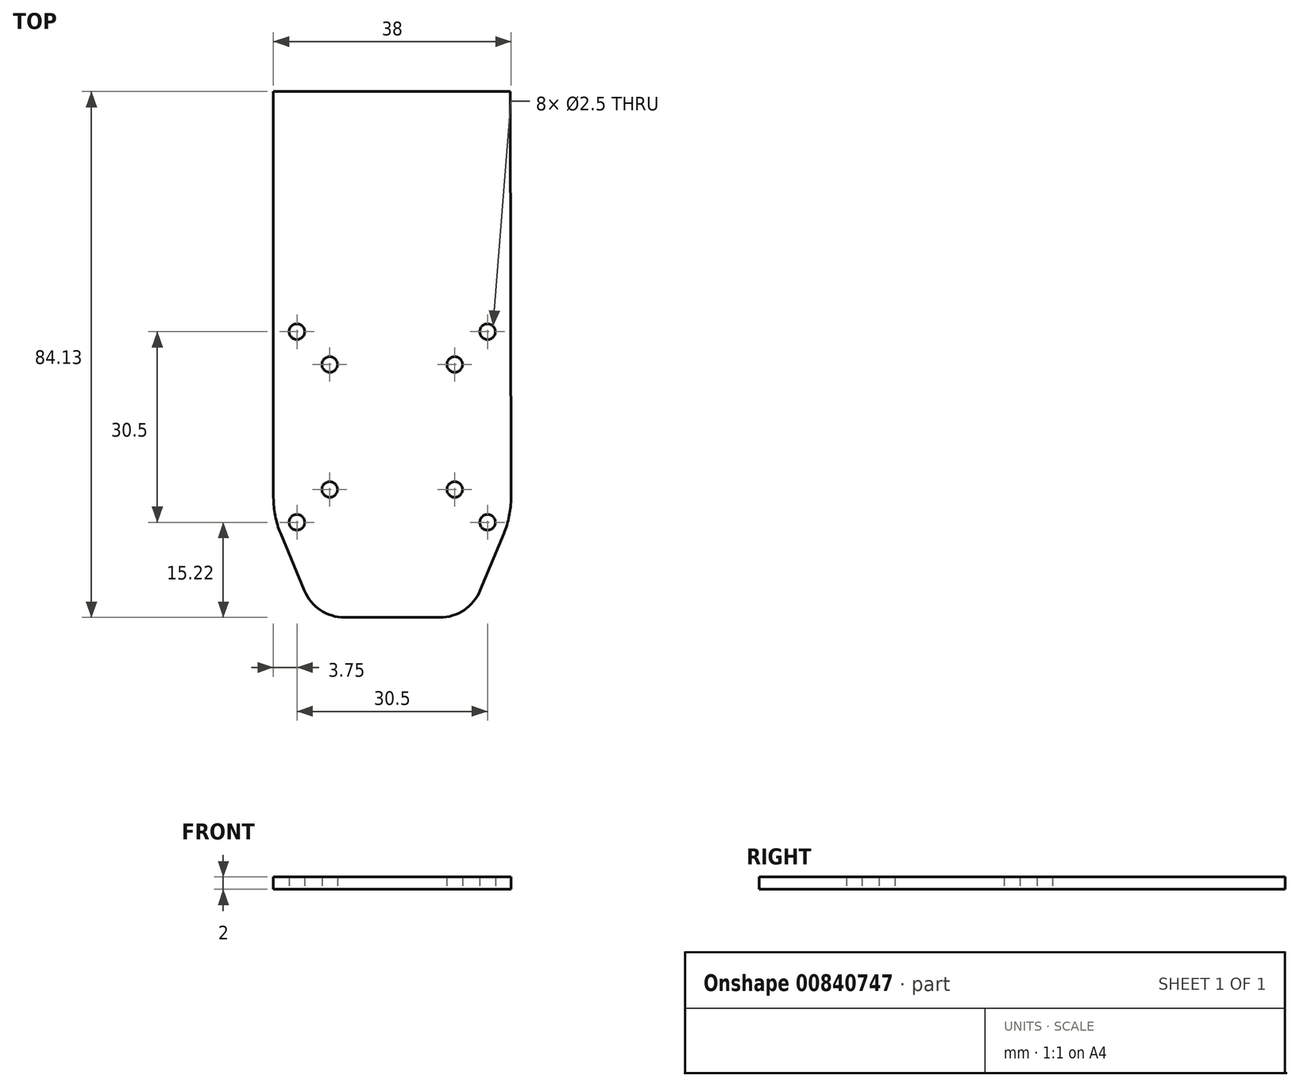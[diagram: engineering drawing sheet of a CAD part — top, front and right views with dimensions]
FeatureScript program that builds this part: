
annotation { "Feature Type Name" : "Feature", "Feature Type Description" : "" }
export const myFeature = defineFeature(function(context is Context, id is Id, definition is map)
    precondition{}
    {
        {
            var Q0;
            Q0=qCreatedBy(makeId("Top.planeOp"),FACE);
            var sketch = newSketch(context, id + "F0", { "sketchPlane" : qUnion([Q0])});
            skLineSegment(sketch, "E0.bottom", {"start": v(10, -10) * mm, "end": v(-10, -10) * mm, "construction": true});
            skLineSegment(sketch, "E0.top", {"start": v(10, 10) * mm, "end": v(-10, 10) * mm, "construction": true});
            skLineSegment(sketch, "E0.left", {"start": v(10, -10) * mm, "end": v(10, 10) * mm, "construction": true});
            skLineSegment(sketch, "E0.right", {"start": v(-10, -10) * mm, "end": v(-10, 10) * mm, "construction": true});
            skPoint(sketch, "E0.middle", {"position": v(0, 0) * mm});
            skCircle(sketch, "E1", {"center": v(-10, 10) * mm, "radius": 1.25 * mm});
            skCircle(sketch, "E2.MirrorC", {"center": v(10, 10) * mm, "radius": 1.25 * mm});
            skCircle(sketch, "E3.MirrorC", {"center": v(10, -10) * mm, "radius": 1.25 * mm});
            skCircle(sketch, "E4.MirrorC", {"center": v(-10, -10) * mm, "radius": 1.25 * mm});
            skPoint(sketch, "E5.right.end.orphan", {"position": v(-13.5, 13.5) * mm});
            skPoint(sketch, "E5.bottom.end.orphan", {"position": v(-13.5, -13.5) * mm});
            skPoint(sketch, "E5.left.end.orphan", {"position": v(13.5, 13.5) * mm});
            skPoint(sketch, "E5.left.start.orphan", {"position": v(13.5, -13.5) * mm});
            skLineSegment(sketch, "E6.bottom", {"start": v(15.25, -15.25) * mm, "end": v(-15.25, -15.25) * mm, "construction": true});
            skLineSegment(sketch, "E6.top", {"start": v(15.25, 15.25) * mm, "end": v(-15.25, 15.25) * mm, "construction": true});
            skLineSegment(sketch, "E6.left", {"start": v(15.25, -15.25) * mm, "end": v(15.25, 15.25) * mm, "construction": true});
            skLineSegment(sketch, "E6.right", {"start": v(-15.25, -15.25) * mm, "end": v(-15.25, 15.25) * mm, "construction": true});
            skCircle(sketch, "E7", {"center": v(-15.25, 15.25) * mm, "radius": 1.25 * mm});
            skCircle(sketch, "E8.MirrorC", {"center": v(15.25, 15.25) * mm, "radius": 1.25 * mm});
            skCircle(sketch, "E9.MirrorC", {"center": v(15.25, -15.25) * mm, "radius": 1.25 * mm});
            skCircle(sketch, "E10.MirrorC", {"center": v(-15.25, -15.25) * mm, "radius": 1.25 * mm});
            skLineSegment(sketch, "E11.top", {"start": v(-19, 53.66) * mm, "end": v(18.87, 53.66) * mm});
            skLineSegment(sketch, "E12", {"start": v(-17.85, -17.05) * mm, "end": v(-14.07, -26.15) * mm});
            skLineSegment(sketch, "E13.MirrorCS", {"start": v(17.85, -17.05) * mm, "end": v(14.07, -26.15) * mm});
            skPoint(sketch, "E14.visualSharp", {"position": v(-19, -14.28) * mm});
            skArc(sketch, "E14.filletArc", {"start": v(-19, -11.3) * mm, "mid": v(-18.71, -14.23) * mm, "end": v(-17.85, -17.05) * mm});
            skArc(sketch, "E15.MirrorCS", {"start": v(19, -11.3) * mm, "mid": v(18.71, -14.23) * mm, "end": v(17.85, -17.05) * mm});
            skLineSegment(sketch, "E16", {"start": v(-19, 53.66) * mm, "end": v(-19, -11.3) * mm});
            skLineSegment(sketch, "E17", {"start": v(18.87, 53.66) * mm, "end": v(19, -11.3) * mm});
            skPoint(sketch, "E18.end.orphan", {"position": v(8.94, -30.47) * mm});
            skPoint(sketch, "E19.orphan", {"position": v(-17.85, -17.05) * mm});
            skPoint(sketch, "E20.visualSharp", {"position": v(12.28, -30.47) * mm});
            skArc(sketch, "E20.filletArc", {"start": v(7.6, -30.47) * mm, "mid": v(11.5, -29.3) * mm, "end": v(14.07, -26.15) * mm});
            skArc(sketch, "E21.MirrorCS", {"start": v(-7.6, -30.47) * mm, "mid": v(-11.5, -29.3) * mm, "end": v(-14.07, -26.15) * mm});
            skLineSegment(sketch, "E22", {"start": v(-7.6, -30.47) * mm, "end": v(7.6, -30.47) * mm});
            skSolve(sketch);
        }
        {
            var Q0;
            Q0 = qSketchRegion(id + "F0", true);
            extrude(context, id + "F1", {"entities" : qUnion([Q0]), "depth" : 2 * mm, "offsetDistance" : 25 * mm});
        }
    });
